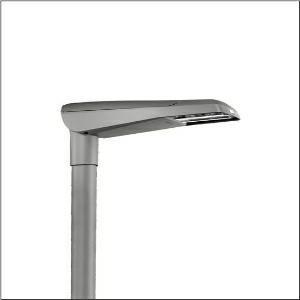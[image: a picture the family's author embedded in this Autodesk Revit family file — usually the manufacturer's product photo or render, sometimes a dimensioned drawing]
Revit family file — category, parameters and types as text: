
# Revit family: streetlight_sl_11_iq_micro___st0_5a_5xc1bc1f08ce_e478
name_source: partatom
category: Lighting Fixtures
units: mm (PartAtom-declared; Revit-internal decimal feet)

## family parameters
Cut with Voids When Loaded = No
Host = Face
Light Source = No
Part Type = Normal
Room Calculation Point = No
Round Connector Dimension = Use Diameter
Shared = No

## types (1)
- --- (1 x LED, 1580 lm, 14 W, 2200K)
    Apparent Load = 14 VA
    CIE Flux Codes = 42 72 97 100 100
    Color Rendering = 70
    Color Temperature = 2200K
    Default Elevation = 1800 mm
    Description = Streetlight SL 11 iQ micro, mast luminaire, primary light control with 3 zone facetted reflector, of plastic, silver coated, highly specular, primary optical cover: cover, of PMMA, transparent, light distribution: ST0.5a, light emission: direct distribution, primary light characteristic: asymmetric, installation type: post-top, side-entry, LED, High Power LED, rated luminous flux: 1.860lm, luminous efficacy: 135lm/W, light colour: 722/727/730/740, colour temperature: 2200/2700/3000/4000K, control gear: iQ Street-Remote, control: Street-Remote, Auto-Match, Temp-Guard, Lumen-Switch, Night-Set, Smart-Wire, Light-Fading, Desk-Remote (wireless, voltage-free reading and setting of iQ features in the workshop via application-optimized NFC function/RFID function), optimised constant luminous flux control (CLO 2.0), with cable H07RN-F 5x 1.5mm², mains connection: 220..240V, AC, 50/60Hz, connection cable pre-assembled, cable length: 5,5m, start of lifetime: 14W, end of service life: 14W, reduction: 8W, luminaire housing, of diecast aluminium, powder-coated, Siteco® metallic grey (DB 702S), please order mast flange separately, inclination adjustable without tools: 0°, 5°, 10°, 15° (post-top) | 0°, -5°, -10°, -15° (side-entry), sealing non-destructively replaceable, multi-level sealing system, length: 600mm, width: 174mm, height: 116mm, mast flange for spigot size: 42mm (side-entry): 5XC10008XM4, 60/48mm (side-entry/post-top): 5XC10108XM2, 76/60mm (side-entry/post-top): 5XC10108XM1, mounting height: 4..8m, equipment: standard, protection rating (complete): IP66, insulation class (complete): insulation class II (safety insulation), certification: CE, ENEC, VDE, impact resistance: IK09, permissible operating ambient temperature for outdoor applications: -25..+50°C, standard-compliant lighting for roads and squares, Environmental Product Declaration (EPD) tested and certified by an independent institute, packaging unit: 1 piece

Light Distribution: ST0.5a
    Height = 116 mm
    Lamp = 1 x LED
    Lamp Light Flux = 1580 lm
    Lamp Power = 14 W
    Lamp count = 1
    Length = 600 mm
    Luminous efficacy = 113 lm/W
    Manufacturer = Siteco
    ModVariant = No
    Model = 5XC1BC1F08CE
    Number of Poles = 1
    OnlyDefault = Yes
    Power Factor = 1
    Product Name = Streetlight SL 11 iQ micro | ST0.5a
    Product group = mast luminaire | pylon top
    ProductGroupID = 6100
    Protection Class = Protection class II
    Protection Degree = IP 66
    RLX_Detail_Level = 1
    RLX_Emergency_Light_Flux = 0 lm
    RLX_Emergency_Type = 0
    RLX_Emergency_Type_DB = No
    RlxData = <blob elided: 58585 chars, md5=6900078c>
    Socket = socket
    Standby Power = 0 W
    System Light Flux = 1580 lm
    System Power = 14 W
    Type Comments = individual setting: luminous flux: 100 % | dim-lin: 254 | 369 mA
    Type Image = l_1006566.jpg
    URL = http://relux.com
    VarID = @adj_032720
    Voltage = 0 V
    Weight = 0.00 kg
    Width = 174 mm

## geometry (parser evidence)
native form markers: Blend x4, Sweep x11
no freeform markers — native parametric forms only
